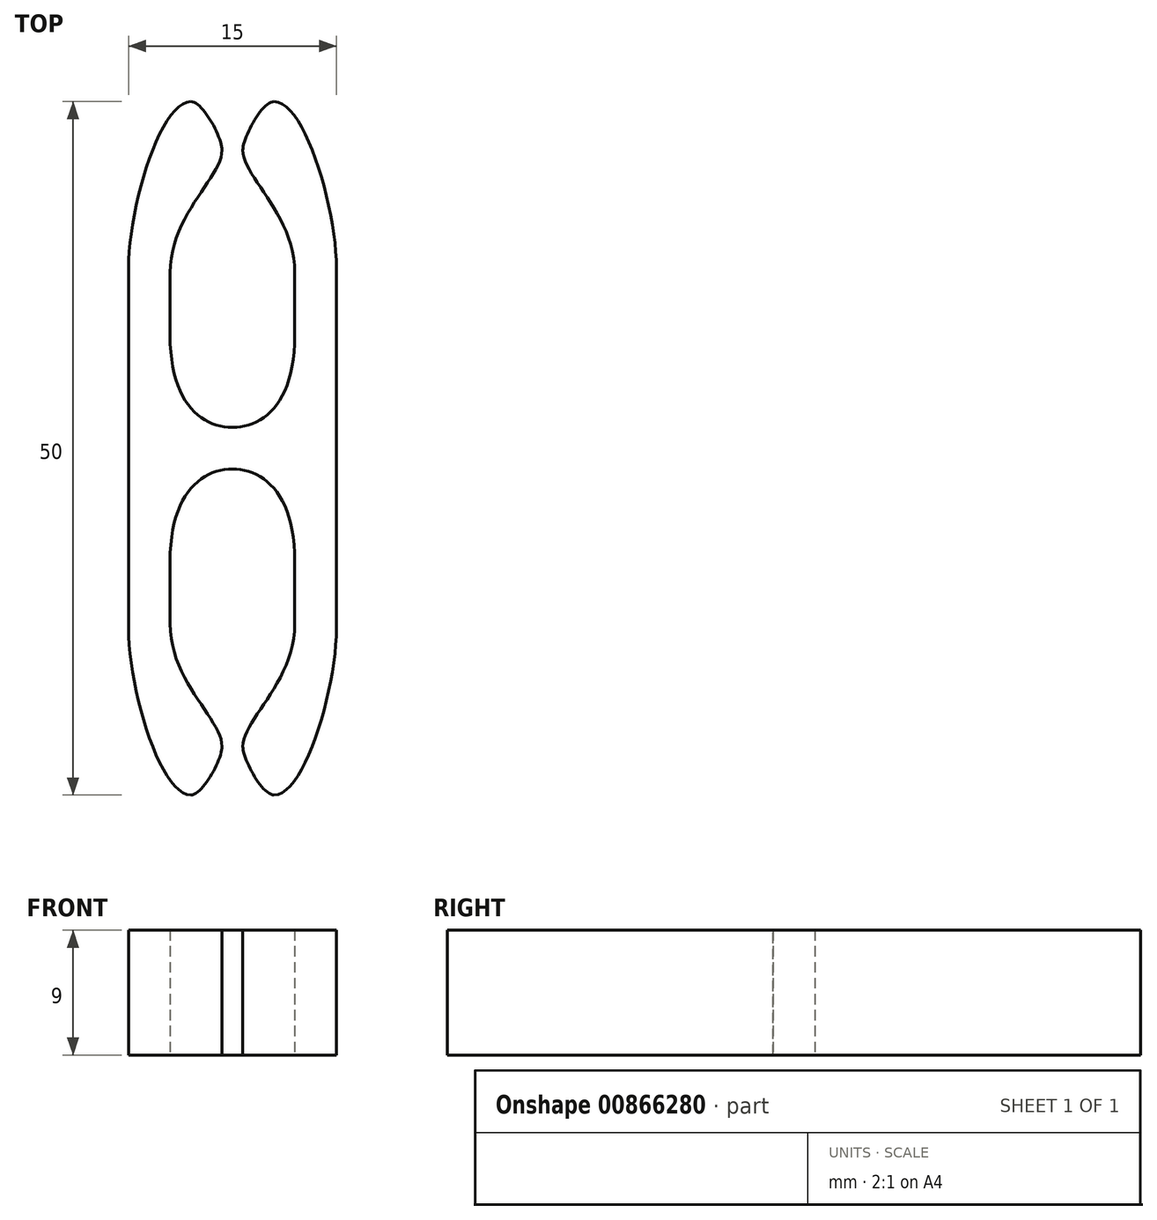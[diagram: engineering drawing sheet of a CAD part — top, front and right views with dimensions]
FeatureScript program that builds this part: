
annotation { "Feature Type Name" : "Feature", "Feature Type Description" : "" }
export const myFeature = defineFeature(function(context is Context, id is Id, definition is map)
    precondition{}
    {
        {
            var Q0;
            Q0=qCreatedBy(makeId("Top.planeOp"),FACE);
            var sketch = newSketch(context, id + "F0", { "sketchPlane" : qUnion([Q0])});
            skLineSegment(sketch, "E0", {"start": v(-7.5, 13) * mm, "end": v(-7.5, 0) * mm});
            skFitSpline(sketch, "E1", {"points": [v(-7.5, 13) * mm, v(-3, 25) * mm], "startDerivative": vector(0, 12.6) * mm, "endDerivative": vector(6.75, 0) * mm});
            skLineSegment(sketch, "E2", {"start": v(-4.5, 8.14) * mm, "end": v(-4.5, 12.66) * mm});
            skFitSpline(sketch, "E3", {"points": [v(4.5, 8.14) * mm, v(0, 1.5) * mm, v(-4.5, 8.14) * mm], "startDerivative": vector(0, -28.85) * mm, "endDerivative": vector(0, 28.85) * mm});
            skFitSpline(sketch, "E4", {"points": [v(-3, 25) * mm, v(-0.75, 21.5) * mm], "startDerivative": vector(2.64, 0) * mm, "endDerivative": vector(0, -2.7) * mm});
            skFitSpline(sketch, "E5", {"points": [v(-0.75, 21.5) * mm, v(-4.5, 12.66) * mm], "startDerivative": vector(0, -5.82) * mm, "endDerivative": vector(0, -12.48) * mm});
            skLineSegment(sketch, "E6", {"start": v(0, 1.5) * mm, "end": v(0, 0) * mm});
            skLineSegment(sketch, "E7", {"start": v(0, 0) * mm, "end": v(-7.5, 0) * mm});
            skSolve(sketch);
        }
        {
            var Q0;
            Q0 = qSketchRegion(id + "F0", true);
            extrude(context, id + "F1", {"entities" : qUnion([Q0]), "endBound" : BoundingType.SYMMETRIC, "depth" : 9 * mm, "offsetDistance" : 25 * mm});
        }
        {
            var Q0;
            Q0=makeQuery(id+"F1.opExtrude","SWEPT_BODY",BODY,{"disambiguationData":[OSD([sQuery(id+"F0.wireOp",EDGE,"E0"),sQuery(id+"F0.wireOp",EDGE,"E1"),sQuery(id+"F0.wireOp",EDGE,"E2"),sQuery(id+"F0.wireOp",EDGE,"E3"),sQuery(id+"F0.wireOp",EDGE,"E4"),sQuery(id+"F0.wireOp",EDGE,"E5"),sQuery(id+"F0.wireOp",EDGE,"E6"),sQuery(id+"F0.wireOp",EDGE,"E7")])]});
            var Q1;
            Q1=makeQuery(id+"F1.opExtrude","SWEPT_FACE",FACE,{"disambiguationData":[OSD([sQuery(id+"F0.wireOp",EDGE,"E6")])]});
            mirror(context, id + "F2", {"operationType" : NewBodyOperationType.ADD, "entities" : qUnion([Q0]), "mirrorPlane" : qUnion([Q1])});
        }
        {
            var Q0;
            Q0=makeQuery(id+"F1.opExtrude","SWEPT_BODY",BODY,{"disambiguationData":[OSD([sQuery(id+"F0.wireOp",EDGE,"E0"),sQuery(id+"F0.wireOp",EDGE,"E1"),sQuery(id+"F0.wireOp",EDGE,"E2"),sQuery(id+"F0.wireOp",EDGE,"E3"),sQuery(id+"F0.wireOp",EDGE,"E4"),sQuery(id+"F0.wireOp",EDGE,"E5"),sQuery(id+"F0.wireOp",EDGE,"E6"),sQuery(id+"F0.wireOp",EDGE,"E7")])]});
            var Q1;
            {var subQ0=makeQuery(id+"F1.opExtrude","SWEPT_FACE",FACE,{"disambiguationData":[OSD([sQuery(id+"F0.wireOp",EDGE,"E7")])]});Q1=makeQuery(id+"F2.boolean.opBoolean","MERGE",FACE,{"derivedFrom":[subQ0,makeQuery(id+"F2.opPattern","COPY",FACE,{"derivedFrom":subQ0,"instanceName":"1"})]});}
            mirror(context, id + "F3", {"operationType" : NewBodyOperationType.ADD, "entities" : qUnion([Q0]), "mirrorPlane" : qUnion([Q1])});
        }
    });
